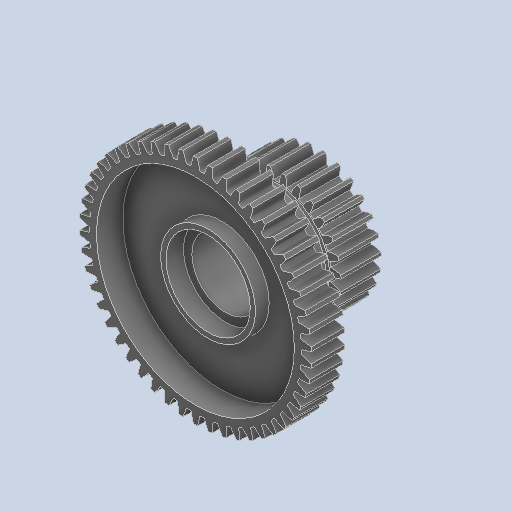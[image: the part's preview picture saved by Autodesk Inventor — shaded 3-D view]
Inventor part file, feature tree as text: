
AUTODESK INVENTOR PART (.ipt)
format: ipt  version: 2023.2 (Build 272271000, 271)  size: 592,896 bytes
history: native  units: in
note: dims shown in document units (in); Inventor stores cm internally (conversion verified against a paired STEP export)
features: chamfer x1
ambient origin geometry x8: Origin, YZ Plane, XZ Plane, XY Plane, X Axis, Y Axis, Z Axis, Center Point
bodies: Solid1 (feature_tree)
feature tree (1):
  chamfer  "Chamfer2"  [1 undecoded]
note: 1 required parameter value undecoded (feature->parameter linkage not recoverable at this tier; creation-order binding heuristic only, values carry confidence <= 0.55)
